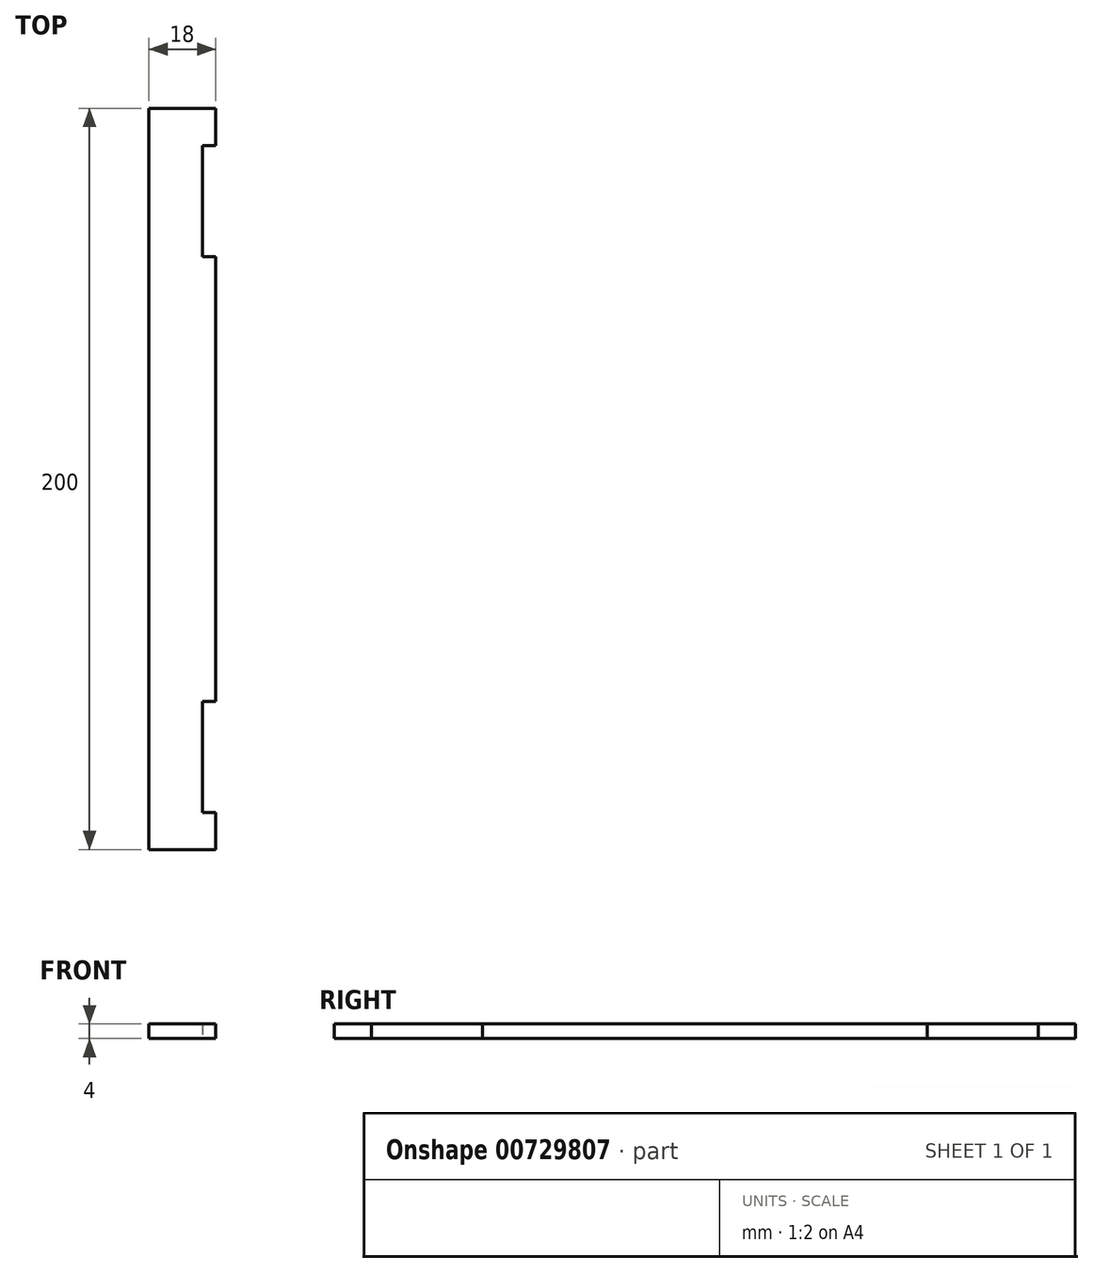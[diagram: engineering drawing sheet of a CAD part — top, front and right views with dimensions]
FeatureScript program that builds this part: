
annotation { "Feature Type Name" : "Feature", "Feature Type Description" : "" }
export const myFeature = defineFeature(function(context is Context, id is Id, definition is map)
    precondition{}
    {
        {
            var Q0;
            Q0=qCreatedBy(makeId("Top.planeOp"),FACE);
            var sketch = newSketch(context, id + "F0", { "sketchPlane" : qUnion([Q0])});
            skLineSegment(sketch, "E0", {"start": v(0, 0) * mm, "end": v(0, 200) * mm, "construction": true});
            skLineSegment(sketch, "E1", {"start": v(0, 200) * mm, "end": v(-5, 200) * mm, "construction": true});
            skLineSegment(sketch, "E2", {"start": v(-5, 200) * mm, "end": v(-68, 200) * mm, "construction": true});
            skLineSegment(sketch, "E3", {"start": v(-68, 200) * mm, "end": v(-68, 190) * mm, "construction": true});
            skLineSegment(sketch, "E4", {"start": v(-68, 0) * mm, "end": v(-5, 0) * mm, "construction": true});
            skLineSegment(sketch, "E5", {"start": v(-5, 0) * mm, "end": v(0, 0) * mm, "construction": true});
            skLineSegment(sketch, "E6", {"start": v(-5, 0) * mm, "end": v(-5, 80) * mm, "construction": true});
            skLineSegment(sketch, "E7", {"start": v(-5, 80) * mm, "end": v(-6.5, 80) * mm, "construction": true});
            skLineSegment(sketch, "E8", {"start": v(-6.5, 80) * mm, "end": v(-6.5, 86.5) * mm, "construction": true});
            skLineSegment(sketch, "E9", {"start": v(-6.5, 86.5) * mm, "end": v(-5, 86.5) * mm, "construction": true});
            skLineSegment(sketch, "E10", {"start": v(-5, 86.5) * mm, "end": v(-5, 96.75) * mm, "construction": true});
            skLineSegment(sketch, "E11", {"start": v(-5, 96.75) * mm, "end": v(-6.5, 96.75) * mm, "construction": true});
            skLineSegment(sketch, "E12", {"start": v(-6.5, 96.75) * mm, "end": v(-6.5, 103.25) * mm, "construction": true});
            skLineSegment(sketch, "E13", {"start": v(-6.5, 103.25) * mm, "end": v(-5, 103.25) * mm, "construction": true});
            skLineSegment(sketch, "E14", {"start": v(-5, 103.25) * mm, "end": v(-5, 113.5) * mm, "construction": true});
            skLineSegment(sketch, "E15", {"start": v(-5, 113.5) * mm, "end": v(-6.5, 113.5) * mm, "construction": true});
            skLineSegment(sketch, "E16", {"start": v(-6.5, 113.5) * mm, "end": v(-6.5, 120) * mm, "construction": true});
            skLineSegment(sketch, "E17", {"start": v(-6.5, 120) * mm, "end": v(-5, 120) * mm, "construction": true});
            skLineSegment(sketch, "E18", {"start": v(-5, 120) * mm, "end": v(-5, 200) * mm, "construction": true});
            skLineSegment(sketch, "E19", {"start": v(-68, 10) * mm, "end": v(-64.5, 10) * mm, "construction": true});
            skLineSegment(sketch, "E20", {"start": v(-64.5, 10) * mm, "end": v(-64.5, 40) * mm, "construction": true});
            skLineSegment(sketch, "E21", {"start": v(-64.5, 40) * mm, "end": v(-68, 40) * mm, "construction": true});
            skLineSegment(sketch, "E22", {"start": v(-68, 160) * mm, "end": v(-64.5, 160) * mm, "construction": true});
            skLineSegment(sketch, "E23", {"start": v(-64.5, 160) * mm, "end": v(-64.5, 190) * mm, "construction": true});
            skLineSegment(sketch, "E24", {"start": v(-64.5, 190) * mm, "end": v(-68, 190) * mm, "construction": true});
            skLineSegment(sketch, "E25.trimOffspring", {"start": v(-68, 160) * mm, "end": v(-68, 40) * mm, "construction": true});
            skLineSegment(sketch, "E26.trimOffspring", {"start": v(-68, 10) * mm, "end": v(-68, 0) * mm, "construction": true});
            skLineSegment(sketch, "E27.bottom", {"start": v(-82, 200) * mm, "end": v(-100, 200) * mm});
            skLineSegment(sketch, "E27.top", {"start": v(-82, 0) * mm, "end": v(-100, 0) * mm});
            skLineSegment(sketch, "E27.left", {"start": v(-82, 200) * mm, "end": v(-82, 190) * mm});
            skLineSegment(sketch, "E27.right", {"start": v(-100, 200) * mm, "end": v(-100, 0) * mm});
            skLineSegment(sketch, "E28", {"start": v(-82, 10) * mm, "end": v(-85.5, 10) * mm});
            skLineSegment(sketch, "E29", {"start": v(-85.5, 40) * mm, "end": v(-85.5, 10) * mm});
            skLineSegment(sketch, "E30", {"start": v(-85.5, 40) * mm, "end": v(-82, 40) * mm});
            skLineSegment(sketch, "E31.trimOffspring", {"start": v(-82, 10) * mm, "end": v(-82, 0) * mm});
            skLineSegment(sketch, "E32", {"start": v(-82, 160) * mm, "end": v(-85.5, 160) * mm});
            skLineSegment(sketch, "E33", {"start": v(-85.5, 160) * mm, "end": v(-85.5, 190) * mm});
            skLineSegment(sketch, "E34", {"start": v(-85.5, 190) * mm, "end": v(-82, 190) * mm});
            skLineSegment(sketch, "E35.trimOffspring", {"start": v(-82, 160) * mm, "end": v(-82, 40) * mm});
            skSolve(sketch);
        }
        {
            var Q0;
            Q0=qSketchRegion(id+"F0",true);
            extrude(context, id + "F1", {"entities" : qUnion([Q0]), "depth" : 4 * mm, "offsetDistance" : 25 * mm});
        }
    });
